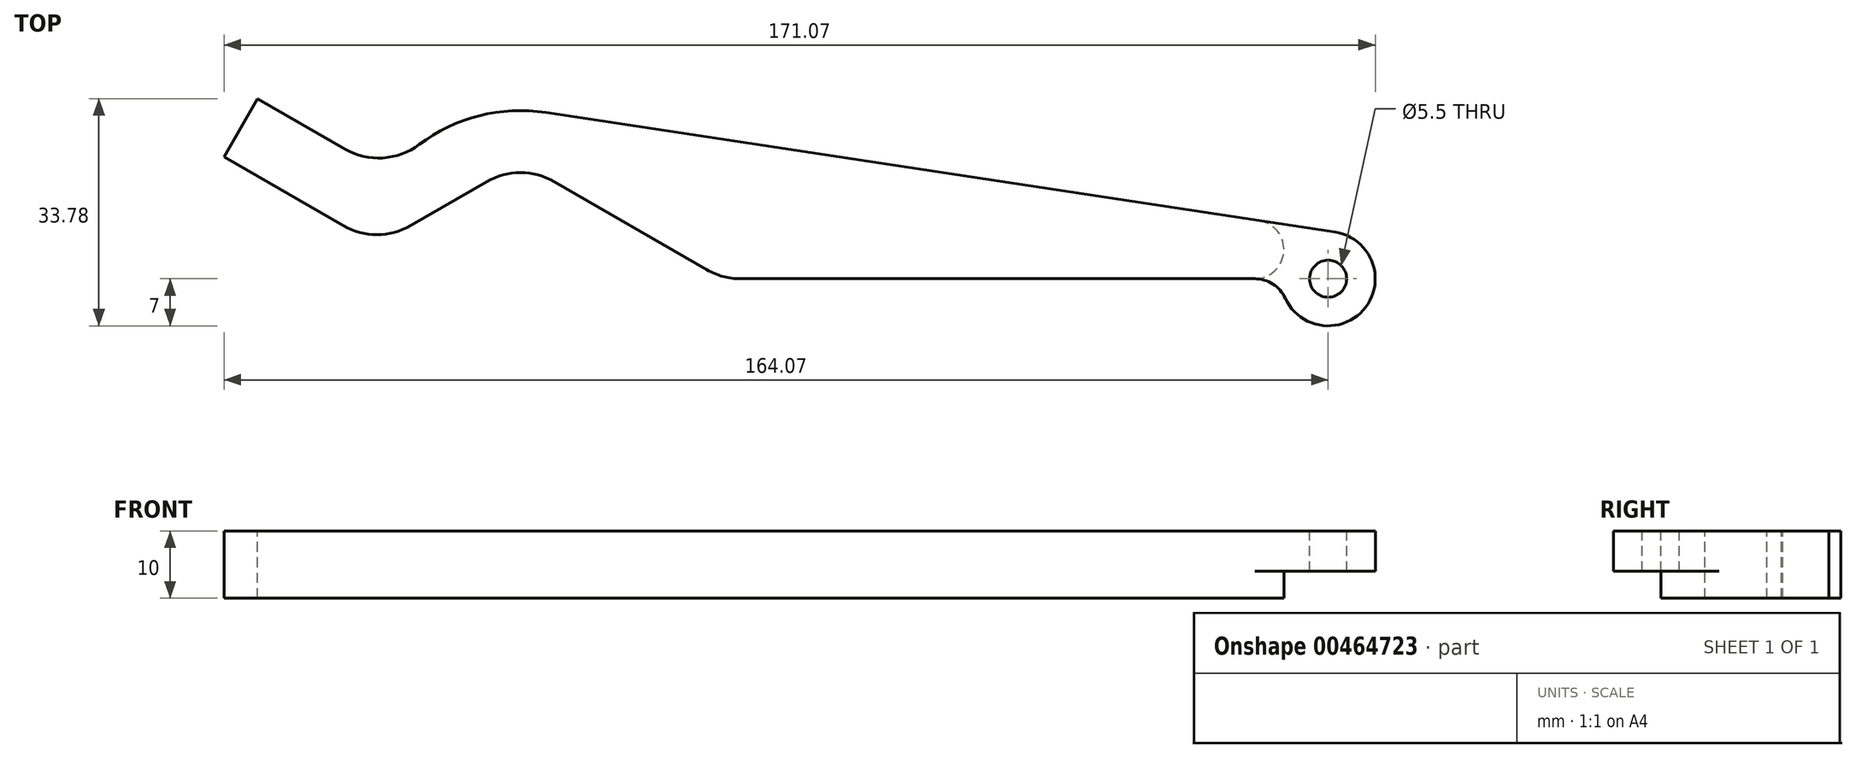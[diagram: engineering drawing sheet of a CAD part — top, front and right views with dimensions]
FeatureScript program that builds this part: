
annotation { "Feature Type Name" : "Feature", "Feature Type Description" : "" }
export const myFeature = defineFeature(function(context is Context, id is Id, definition is map)
    precondition{}
    {
        {
            var Q0;
            Q0=qCreatedBy(makeId("Top.planeOp"),FACE);
            var sketch = newSketch(context, id + "F0", { "sketchPlane" : qUnion([Q0])});
            skCircle(sketch, "E0", {"center": v(0, 0) * mm, "radius": 2 * mm, "construction": true});
            skArc(sketch, "E1", {"start": v(-6.36, -2.92) * mm, "mid": v(5.6, -4.21) * mm, "end": v(1.05, 6.92) * mm});
            skCircle(sketch, "E2", {"center": v(-120, 0) * mm, "radius": 15 * mm, "construction": true});
            skLineSegment(sketch, "E3", {"start": v(-116.25, 24.72) * mm, "end": v(1.05, 6.92) * mm});
            skArc(sketch, "E4", {"start": v(-116.25, 24.72) * mm, "mid": v(-126.13, 24.24) * mm, "end": v(-135.05, 19.96) * mm});
            skLineSegment(sketch, "E5", {"start": v(-115, 14.43) * mm, "end": v(-92.32, 1.34) * mm});
            skLineSegment(sketch, "E6", {"start": v(-125, 14.43) * mm, "end": v(-136.34, 7.89) * mm});
            skLineSegment(sketch, "E7", {"start": v(-146.08, 19.28) * mm, "end": v(-159.07, 26.78) * mm});
            skLineSegment(sketch, "E8", {"start": v(-159.07, 26.78) * mm, "end": v(-164.07, 18.12) * mm});
            skLineSegment(sketch, "E9", {"start": v(-164.07, 18.12) * mm, "end": v(-146.34, 7.89) * mm});
            skPoint(sketch, "E10.visualSharp", {"position": v(-139.46, 15.46) * mm});
            skArc(sketch, "E10.filletArc", {"start": v(-146.08, 19.28) * mm, "mid": v(-140.46, 17.96) * mm, "end": v(-135.05, 19.96) * mm});
            skPoint(sketch, "E11.visualSharp", {"position": v(-141.34, 5) * mm});
            skArc(sketch, "E11.filletArc", {"start": v(-146.34, 7.89) * mm, "mid": v(-141.34, 6.55) * mm, "end": v(-136.34, 7.89) * mm});
            skPoint(sketch, "E12.visualSharp", {"position": v(-120, 17.32) * mm});
            skArc(sketch, "E12.filletArc", {"start": v(-115, 14.43) * mm, "mid": v(-120, 15.77) * mm, "end": v(-125, 14.43) * mm});
            skLineSegment(sketch, "E13", {"start": v(-87.32, 0) * mm, "end": v(-10.9, 0) * mm});
            skLineSegment(sketch, "E14", {"start": v(0, 0) * mm, "end": v(-7, 0) * mm, "construction": true});
            skPoint(sketch, "E15.visualSharp", {"position": v(-90, 0) * mm});
            skArc(sketch, "E15.filletArc", {"start": v(-92.32, 1.34) * mm, "mid": v(-89.9, 0.34) * mm, "end": v(-87.32, 0) * mm});
            skPoint(sketch, "E16.visualSharp", {"position": v(-7, 0) * mm});
            skArc(sketch, "E16.filletArc", {"start": v(-6.36, -2.92) * mm, "mid": v(-8.2, -0.8) * mm, "end": v(-10.9, 0) * mm});
            skSolve(sketch);
        }
        {
            var Q0;
            Q0 = qSketchRegion(id + "F0", true);
            extrude(context, id + "F1", {"entities" : qUnion([Q0]), "oppositeDirection" : true, "depth" : 10 * mm});
        }
        {
            var Q0;
            Q0=makeQuery(id+"F1.opExtrude","CAP_FACE",FACE,{"disambiguationData":[OSD([sQuery(id+"F0.wireOp",EDGE,"E1"),sQuery(id+"F0.wireOp",EDGE,"E3"),sQuery(id+"F0.wireOp",EDGE,"E4"),sQuery(id+"F0.wireOp",EDGE,"E5"),sQuery(id+"F0.wireOp",EDGE,"E6"),sQuery(id+"F0.wireOp",EDGE,"E7"),sQuery(id+"F0.wireOp",EDGE,"E8"),sQuery(id+"F0.wireOp",EDGE,"E9"),sQuery(id+"F0.wireOp",EDGE,"E10.filletArc"),sQuery(id+"F0.wireOp",EDGE,"E11.filletArc"),sQuery(id+"F0.wireOp",EDGE,"E12.filletArc"),sQuery(id+"F0.wireOp",EDGE,"E13"),sQuery(id+"F0.wireOp",EDGE,"E15.filletArc"),sQuery(id+"F0.wireOp",EDGE,"E16.filletArc")])],"isStart":true});
            var sketch = newSketch(context, id + "F2", { "sketchPlane" : qUnion([Q0])});
            skPoint(sketch, "E17", {"position": v(0, 0) * mm});
            skSolve(sketch);
        }
        {
            var Q0;
            Q0=sQuery(id+"F2.wireOp",VERTEX,"E17");
            var Q1;
            Q1=makeQuery(id+"F1.opExtrude","SWEPT_BODY",BODY,{"disambiguationData":[OSD([sQuery(id+"F0.wireOp",EDGE,"E1"),sQuery(id+"F0.wireOp",EDGE,"E3"),sQuery(id+"F0.wireOp",EDGE,"E4"),sQuery(id+"F0.wireOp",EDGE,"E5"),sQuery(id+"F0.wireOp",EDGE,"E6"),sQuery(id+"F0.wireOp",EDGE,"E7"),sQuery(id+"F0.wireOp",EDGE,"E8"),sQuery(id+"F0.wireOp",EDGE,"E9"),sQuery(id+"F0.wireOp",EDGE,"E10.filletArc"),sQuery(id+"F0.wireOp",EDGE,"E11.filletArc"),sQuery(id+"F0.wireOp",EDGE,"E12.filletArc"),sQuery(id+"F0.wireOp",EDGE,"E13"),sQuery(id+"F0.wireOp",EDGE,"E15.filletArc"),sQuery(id+"F0.wireOp",EDGE,"E16.filletArc")])]});
            hole(context, id + "F3", {"style" : HoleStyle.SIMPLE, "endStyle" : HoleEndStyle.THROUGH, "standardTappedOrClearance" : lookupTablePath({ "standard" : "ISO", "fit" : "Normal", "size" : "M5", "type" : "Clearance" }), "standardBlindInLast" : lookupTablePath({ "fit" : "Standard", "standard" : "ISO", "size" : "M5", "type" : "Clearance" }), "holeDiameter" : 5.5 * mm, "isTappedThrough" : true, "tappedDepth" : 12 * mm, "tapClearance" : 3, "locations" : qUnion([Q0]), "scope" : qUnion([Q1])});
        }
        {
            var Q0;
            Q0=makeQuery(id+"F1.opExtrude","CAP_FACE",FACE,{"disambiguationData":[OSD([sQuery(id+"F0.wireOp",EDGE,"E1"),sQuery(id+"F0.wireOp",EDGE,"E3"),sQuery(id+"F0.wireOp",EDGE,"E4"),sQuery(id+"F0.wireOp",EDGE,"E5"),sQuery(id+"F0.wireOp",EDGE,"E6"),sQuery(id+"F0.wireOp",EDGE,"E7"),sQuery(id+"F0.wireOp",EDGE,"E8"),sQuery(id+"F0.wireOp",EDGE,"E9"),sQuery(id+"F0.wireOp",EDGE,"E10.filletArc"),sQuery(id+"F0.wireOp",EDGE,"E11.filletArc"),sQuery(id+"F0.wireOp",EDGE,"E12.filletArc"),sQuery(id+"F0.wireOp",EDGE,"E13"),sQuery(id+"F0.wireOp",EDGE,"E15.filletArc"),sQuery(id+"F0.wireOp",EDGE,"E16.filletArc")])],"isStart":false});
            var sketch = newSketch(context, id + "F4", { "sketchPlane" : qUnion([Q0])});
            skLineSegment(sketch, "E18.0", {"start": v(-87.32, 0) * mm, "end": v(-10.9, 0) * mm});
            skArc(sketch, "E19", {"start": v(-10.26, -8.64) * mm, "mid": v(-6.58, -4.02) * mm, "end": v(-10.9, 0) * mm});
            skLineSegment(sketch, "E20.0", {"start": v(-10.26, -8.64) * mm, "end": v(1.05, -6.92) * mm});
            skArc(sketch, "E21.0", {"start": v(-6.36, 2.92) * mm, "mid": v(5.6, 4.21) * mm, "end": v(1.05, -6.92) * mm});
            skArc(sketch, "E22.0", {"start": v(-6.36, 2.92) * mm, "mid": v(-8.2, 0.8) * mm, "end": v(-10.9, 0) * mm});
            skPoint(sketch, "E23.orphan", {"position": v(-116.25, -24.72) * mm});
            skSolve(sketch);
        }
        {
            var Q0;
            Q0 = qSketchRegion(id + "F4", true);
            extrude(context, id + "F5", {"entities" : qUnion([Q0]), "operationType" : NewBodyOperationType.REMOVE, "oppositeDirection" : true, "depth" : 4 * mm});
        }
    });
